# Revit family: HERZ Strömax Commissioning Valve With Test Points 4217 GN
name_source: partatom
category: Rohrzubehör
units: mm (PartAtom-declared; Revit-internal decimal feet)

## family parameters
Arbeitsebenenbasiert = Nein
Beim Laden mit Abzugskörper schneiden = Nein
Bemaßung runder Anschluss = Durchmesser verwenden
Gemeinsam genutzt = Nein
Immer vertikal = Ja
OmniClass-Nummer = 23.65.55.14
OmniClass-Titel = Valves for Liquid Services
Teiletyp = Unterbricht

## types (1)
- HERZ Strömax Commissioning Valve With Test Points 4217 GN
    Body = brass CW602N
    D04 = 16.25 mm  [stored 0.0533136 ft]
    D05 = 16.75 mm
    Differential pressure measurement = STRÖMAX-GN commissioning valve is equipped with two test points.
The differential pressure can be measured using a suitable measuring instrument, which permits calculation of the flow rate as a function of the respective presetting step.
The HERZ-Measuring computer (1 8900 05) permits direct flow rate reading (consult the equipment manual).
    Field of application = For hydraulic balancing in heating and cooling systems, adjustment of distribution mains, circuits, heat exchangers, heating and cooling registers, etc.
Close the valve clockwise.
    H01 = 41.5 mm  [stored 0.136155 ft]
    Hand wheel = Polyamide, red
    Hersteller = HERZ Armaturen Ges.m.b.H.
    Installation position = The non-rising valve spindle arranged perpendicular to the valve axis guarantees optimum accessibility and optimum valve operation in any installation position.
    Internal threaded connectors = acc. ISO 7/1
    MD01 = 7.4 mm  [stored 0.0242782 ft]
    Max. operating pressure = 2500000.0 Pa
    Max. operating temperature (from DN40) = 110 °C
    Max. operating temperature (up to DN32) = 130 °C
    Medium = Water purity in accordance with the OeNORM H5195 and VDI 2035 standards.
Ethylene and propylene glycol can be mixed to a ratio of 25 - 50 vol. %.
    Model = STRÖMAX-GN commissioning valve with equal percentage characteristic graph and test points, 1/2′′ – 2′′.
Screw down model, brass version, socket x socket, non-rising spindle, spindle seal by means of double-O-ring, presetting by limitation of valve lift by means of internal spindle;
display of presetting step on the handwheel shaft.
    S02 = 60 mm  [stored 0.19685 ft]
    SCRNCODE = 05;07;02
    SCRNSEQ = ARM;ARM_TYP="STRV";2
    SC_NennweiteBerechnet = 0
    Spindle = brass CW617N
    Spindle seals = EPDM
    URL = www.herzvalves.com
    Vorgabe-Ansicht = 0 mm  [stored 0 ft]
    W01 = 30.00°
    W02 = 60.00°

note: [stored X ft] marks values corroborated as IEEE doubles in the binary element streams (Revit-internal decimal feet)
